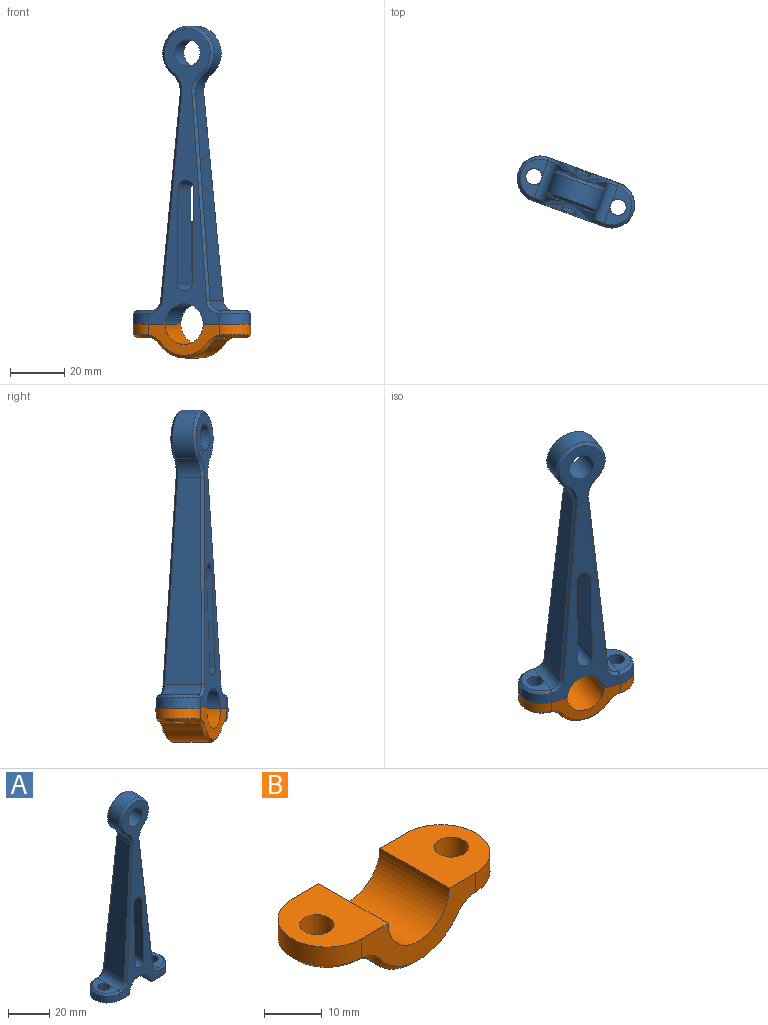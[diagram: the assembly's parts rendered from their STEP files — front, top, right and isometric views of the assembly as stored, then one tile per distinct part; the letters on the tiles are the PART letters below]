
ASSEMBLY  parts=2 mates=1
PART A: 49 faces, bbox 46x17.7x111 mm
  f0: plane 109.52x28.52mm, normal (0,1,0.03), area 892.8mm2, adj f2,f12,f13,f14,f19,f22,f24,f26
  f1: plane 109.7x28.7mm, normal (0,-1,0.03), area 893.5mm2, adj f2,f12,f13,f14,f20,f21,f27,f29
  f2: plane 17.12x15.12mm, normal (0,0,-1), area 195.9mm2, adj f0,f1,f13,f17,f18,f19,f20
  f3: plane 14.69x7.82mm, normal (0,0,1), area 62.2mm2, adj f11,f15,f23,f24,f25,f27
  f4: plane 14.69x7.82mm, normal (0,0,1), area 62.2mm2, adj f5,f17,f40,f42,f43,f44
  f5: cylinder r=4mm len=14.65mm, axis (0,1,0), area 86mm2, adj f4,f6,f18,f38,f41
  f6: plane 76.38x14.33mm, normal (-1,0,0.09), area 894.2mm2, adj f5,f7,f36,f39
  f7: cylinder r=8mm len=9mm, axis (0,1,0), area 69.9mm2, adj f6,f8,f34,f37
  f8: cylinder r=10mm len=20mm, axis (0,1,0), area 419.7mm2, adj f7,f9,f32,f35
  f9: cylinder r=8mm len=9mm, axis (0,1,0), area 69.9mm2, adj f8,f10,f30,f33
  f10: plane 76.38x14.33mm, normal (1,0,0.09), area 894.2mm2, adj f9,f11,f28,f31
  f11: cylinder r=4mm len=14.65mm, axis (0,1,0), area 86mm2, adj f3,f10,f16,f26,f29
  f12: plane 17.12x15.12mm, normal (0,0,-1), area 195.9mm2, adj f0,f1,f13,f15,f16,f21,f22
  f13: cylinder r=7.5mm len=17mm, axis (0,1,0), area 400.6mm2, adj f0,f1,f2,f12
  f14: cylinder r=5mm len=10.02mm, axis (0,1,0), area 309.2mm2, adj f0,f1
  f15: cylinder r=3mm len=6mm, axis (0,0,1), area 84.2mm2, adj f3,f12,f16
  f16: plane 5x1.98mm, normal (1,0,0), area 9.9mm2, adj f11,f12,f15
  f17: cylinder r=3mm len=6mm, axis (0,0,1), area 84.2mm2, adj f2,f4,f18
  f18: plane 5x1.98mm, normal (-1,0,0), area 9.9mm2, adj f2,f5,f17
  f19: cylinder r=8.5mm len=8.64mm, axis (0,0.03,-1), area 52.9mm2, adj f0,f2,f20,f42
  f20: cylinder r=8.5mm len=8.64mm, axis (0,0.03,1), area 52.9mm2, adj f1,f2,f19,f44
  f21: cylinder r=8.5mm len=8.64mm, axis (0,0.03,1), area 52.9mm2, adj f1,f12,f22,f25
  f22: cylinder r=8.5mm len=8.64mm, axis (0,0.03,-1), area 52.9mm2, adj f0,f12,f21,f23
  f23: bspline ~9.04x8.64mm, area 17.9mm2, adj f3,f22,f24,f25
  f24: plane 1.04x1mm, normal (0,0.69,0.72), area 0.5mm2, adj f0,f3,f23,f26
  f25: bspline ~9.04x8.64mm, area 17.9mm2, adj f3,f21,f23,f27
  f26: bspline ~5.02x4.66mm, area 9.7mm2, adj f0,f11,f24,f28
  f27: plane 1.04x1mm, normal (0,-0.69,0.72), area 0.5mm2, adj f1,f3,f25,f29
  f28: plane 76.43x7.71mm, normal (0.7,0.71,0.09), area 112.2mm2, adj f0,f10,f26,f30
  f29: bspline ~5.02x4.66mm, area 9.7mm2, adj f1,f11,f27,f31
  f30: bspline ~7.95x4.41mm, area 12.6mm2, adj f0,f9,f28,f32
  f31: plane 76.43x7.71mm, normal (0.7,-0.71,0.09), area 112.2mm2, adj f1,f10,f29,f33
  f32: bspline ~20.34x17.93mm, area 68.8mm2, adj f0,f8,f30,f34
  f33: bspline ~7.95x4.41mm, area 12.6mm2, adj f1,f9,f31,f35
  f34: bspline ~7.95x4.41mm, area 12.6mm2, adj f0,f7,f32,f36
  f35: bspline ~20.34x17.93mm, area 68.8mm2, adj f1,f8,f33,f37
  f36: plane 76.43x7.71mm, normal (-0.7,0.71,0.09), area 112.2mm2, adj f0,f6,f34,f38
  f37: bspline ~7.95x4.41mm, area 12.6mm2, adj f1,f7,f35,f39
  f38: bspline ~5.02x4.66mm, area 9.7mm2, adj f0,f5,f36,f40
  f39: plane 76.43x7.71mm, normal (-0.7,-0.71,0.09), area 112.2mm2, adj f1,f6,f37,f41
  f40: plane 1.04x1mm, normal (0,0.69,0.72), area 0.5mm2, adj f0,f4,f38,f42
  f41: bspline ~5.02x4.66mm, area 9.7mm2, adj f1,f5,f39,f43
  f42: bspline ~9.04x8.64mm, area 17.9mm2, adj f4,f19,f40,f44
  f43: plane 1.04x1mm, normal (0,-0.69,0.72), area 0.5mm2, adj f1,f4,f41,f44
  f44: bspline ~9.04x8.64mm, area 17.9mm2, adj f4,f20,f42,f43
  f45: cylinder r=3mm len=16.06mm, axis (0,-1,0.03), area 150.4mm2, adj f0,f1,f46,f48
  f46: plane 35.54x15.95mm, normal (-1,0,0), area 515.8mm2, adj f0,f1,f45,f47
  f47: cylinder r=3mm len=13.61mm, axis (0,-1,0.03), area 127.4mm2, adj f0,f1,f46,f48
  f48: plane 35.54x15.95mm, normal (1,0,0), area 515.8mm2, adj f0,f1,f45,f47
PART B: 32 faces, bbox 45x17x12.5 mm
  f0: cylinder r=5mm len=5.4mm, axis (0,1,0), area 22.3mm2, adj f1,f4,f5,f25,f27,f30
  f1: bspline ~4.73x4.32mm, area 8.6mm2, adj f0,f2,f4,f30
  f2: cylinder r=5mm len=5.4mm, axis (0,1,0), area 22.3mm2, adj f1,f4,f5,f26,f28,f30
  f3: plane 14.98x10mm, normal (0,0,-1), area 73.2mm2, adj f14,f15,f17,f18,f31
  f4: cylinder r=12.5mm len=20.52mm, axis (0,1,0), area 361mm2, adj f0,f1,f2,f15,f16,f17,f23,f24
  f5: plane 14.98x10mm, normal (0,0,-1), area 73.2mm2, adj f0,f2,f13,f29,f30
  f6: plane 17x15mm, normal (0,0,1), area 195.7mm2, adj f7,f9,f10,f11,f13
  f7: cylinder r=7.5mm len=17mm, axis (0,1,0), area 400.6mm2, adj f6,f8,f9,f10
  f8: plane 17x15mm, normal (0,0,1), area 195.7mm2, adj f7,f9,f10,f12,f14
  f9: plane 28x11.5mm, normal (0,-1,0), area 145mm2, adj f6,f7,f8,f11,f12,f22,f24,f26
  f10: plane 28x11.5mm, normal (0,1,0), area 145mm2, adj f6,f7,f8,f11,f12,f21,f23,f25
  f11: cylinder r=8.5mm len=17mm, axis (0,0,-1), area 106.8mm2, adj f6,f9,f10,f27,f28,f29
  f12: cylinder r=8.5mm len=17mm, axis (0,0,1), area 106.8mm2, adj f8,f9,f10,f18,f19,f20
  f13: cylinder r=3mm len=6mm, axis (0,0,1), area 94.2mm2, adj f5,f6
  f14: cylinder r=3mm len=6mm, axis (0,0,1), area 94.2mm2, adj f3,f8
  f15: cylinder r=5mm len=5.4mm, axis (0,1,0), area 22.3mm2, adj f3,f4,f16,f19,f21,f31
  f16: bspline ~4.73x4.32mm, area 8.6mm2, adj f4,f15,f17,f31
  f17: cylinder r=5mm len=5.4mm, axis (0,1,0), area 22.3mm2, adj f3,f4,f16,f20,f22,f31
  f18: cone r=7.5mm half-angle=45deg, axis (0,0,1), area 34.5mm2, adj f3,f12,f19,f20
  f19: bspline ~1.01x1.01mm, area 0.5mm2, adj f12,f15,f18,f21
  f20: bspline ~1.01x1.01mm, area 0.5mm2, adj f12,f17,f18,f22
  f21: cone r=6mm half-angle=45deg, axis (0,1,0), area 7mm2, adj f10,f15,f19,f23
  f22: cone r=6mm half-angle=45deg, axis (0,-1,0), area 7mm2, adj f9,f17,f20,f24
  f23: cone r=12.5mm half-angle=45deg, axis (0,-1,0), area 32.7mm2, adj f4,f10,f21,f25
  f24: cone r=11.5mm half-angle=45deg, axis (0,1,0), area 32.7mm2, adj f4,f9,f22,f26
  f25: cone r=6mm half-angle=45deg, axis (0,1,0), area 7mm2, adj f0,f10,f23,f27
  f26: cone r=6mm half-angle=45deg, axis (0,-1,0), area 7mm2, adj f2,f9,f24,f28
  f27: bspline ~1.01x1.01mm, area 0.5mm2, adj f0,f11,f25,f29
  f28: bspline ~1.01x1.01mm, area 0.5mm2, adj f2,f11,f26,f29
  f29: cone r=7.5mm half-angle=45deg, axis (0,0,1), area 34.5mm2, adj f5,f11,f27,f28
  f30: cylinder r=5mm len=9.04mm, axis (0,0,1), area 4.8mm2, adj f0,f1,f2,f5
  f31: cylinder r=5mm len=9.04mm, axis (0,0,1), area 4.8mm2, adj f3,f15,f16,f17
PLACE A rot(axis=(0,0,-1),20deg) t=(9.77,11.49,-46.04)mm
PLACE B rot(axis=(0,0,-1),20deg) t=(9.77,11.49,-46.04)mm
MATE fastened B.f13 <-> A.f15  axis (0,0,1) through (25.28,5.84,-46.04)mm
